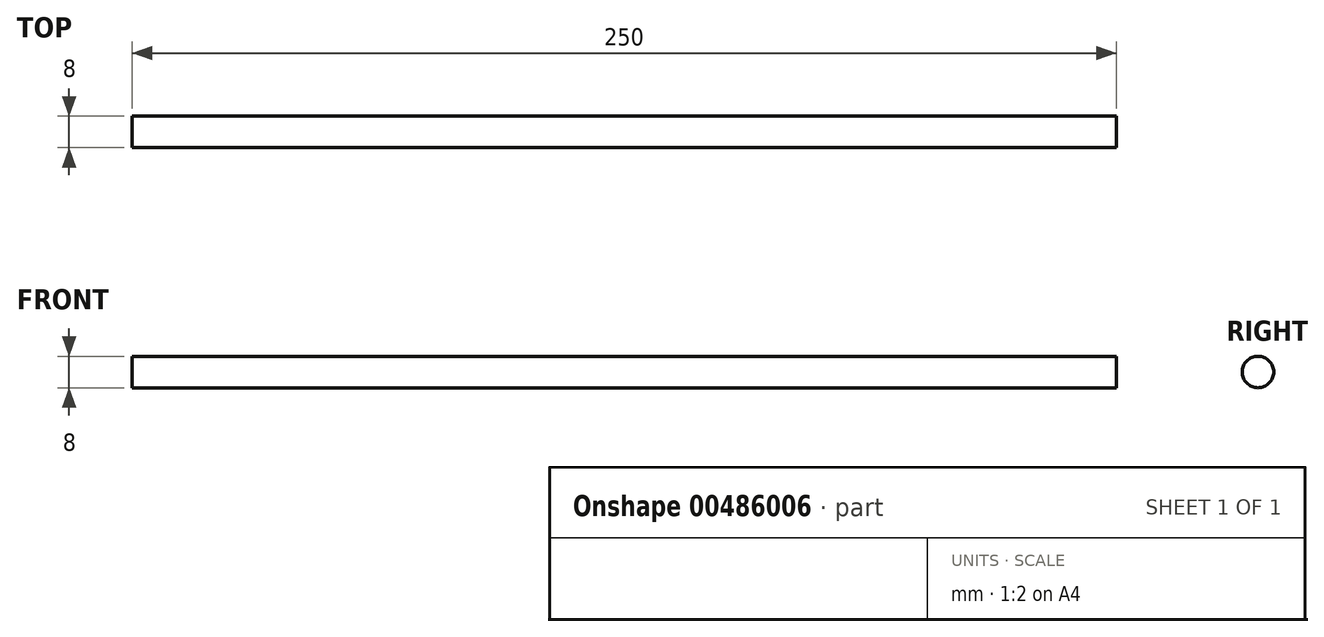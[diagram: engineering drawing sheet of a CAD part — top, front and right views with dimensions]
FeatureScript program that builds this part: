
annotation { "Feature Type Name" : "Feature", "Feature Type Description" : "" }
export const myFeature = defineFeature(function(context is Context, id is Id, definition is map)
    precondition{}
    {
        {
            var Q0;
            Q0=qCreatedBy(makeId("Right.planeOp"),FACE);
            var sketch = newSketch(context, id + "F0", { "sketchPlane" : qUnion([Q0])});
            skCircle(sketch, "E0", {"center": v(0, 0) * mm, "radius": 4 * mm});
            skSolve(sketch);
        }
        {
            var Q0;
            Q0=makeQuery(id+"F0.imprint","IMPRINT",FACE,{"disambiguationData":[TD([[makeQuery(id+"F0.imprint","IMPRINT",EDGE,{"derivedFrom":sQuery(id+"F0.wireOp",EDGE,"E0")}),1.0]])]});
            extrude(context, id + "F1", {"entities" : qUnion([Q0]), "endBound" : BoundingType.SYMMETRIC, "depth" : 250 * mm, "offsetDistance" : 25 * mm});
        }
    });
